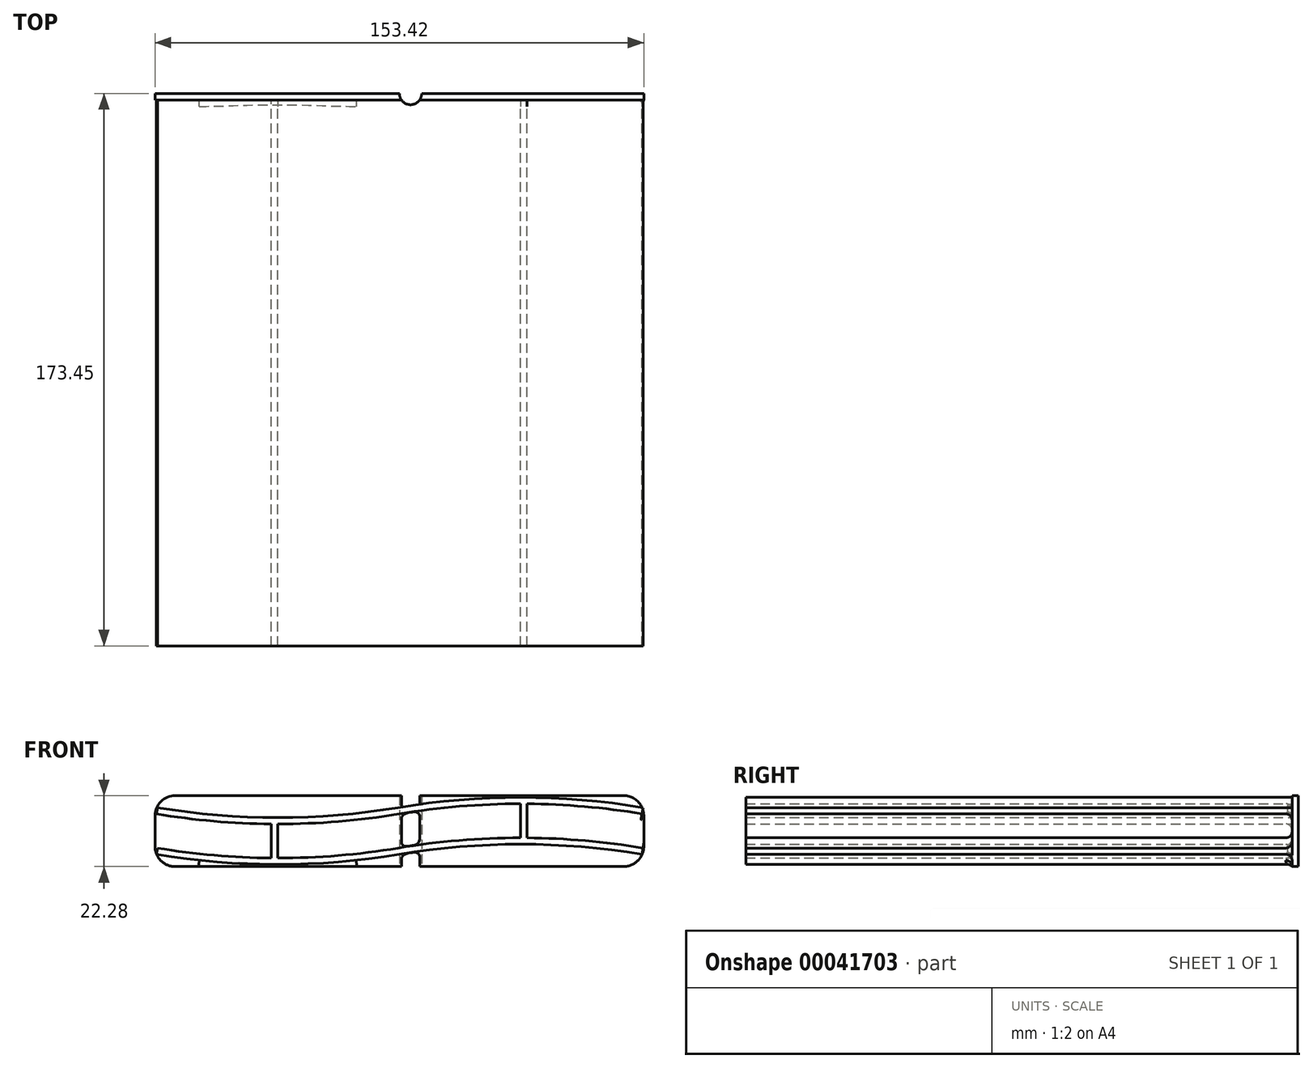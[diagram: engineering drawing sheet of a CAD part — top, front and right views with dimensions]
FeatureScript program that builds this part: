
annotation { "Feature Type Name" : "Feature", "Feature Type Description" : "" }
export const myFeature = defineFeature(function(context is Context, id is Id, definition is map)
    precondition{}
    {
        {
            var Q0;
            Q0=qCreatedBy(makeId("Front.planeOp"),FACE);
            var sketch = newSketch(context, id + "F0", { "sketchPlane" : qUnion([Q0])});
            skLineSegment(sketch, "E0", {"start": v(-48.97, -43) * mm, "end": v(27.23, -43) * mm, "construction": true});
            skLineSegment(sketch, "E1", {"start": v(27.23, -43) * mm, "end": v(103.43, -43) * mm, "construction": true});
            skPoint(sketch, "E2.1.internal.snap0", {"position": v(-10.87, -43) * mm});
            skPoint(sketch, "E2.3.internal.snap0", {"position": v(65.33, -43) * mm});
            skArc(sketch, "E3", {"start": v(-48.97, -43) * mm, "mid": v(-10.87, -46.18) * mm, "end": v(27.23, -43) * mm});
            skPoint(sketch, "E4", {"position": v(-10.87, -46.18) * mm});
            skArc(sketch, "E5", {"start": v(103.43, -43) * mm, "mid": v(65.33, -39.83) * mm, "end": v(27.23, -43) * mm});
            skPoint(sketch, "E6", {"position": v(65.33, -39.83) * mm});
            skArc(sketch, "E7.0", {"start": v(103.76, -41.03) * mm, "mid": v(85.6, -38.72) * mm, "end": v(67.33, -37.84) * mm});
            skArc(sketch, "E7.1", {"start": v(-48.64, -41.03) * mm, "mid": v(-30.82, -43.3) * mm, "end": v(-12.87, -44.17) * mm});
            skLineSegment(sketch, "E8", {"start": v(-48.64, -41.03) * mm, "end": v(-48.97, -43) * mm});
            skLineSegment(sketch, "E9", {"start": v(103.76, -41.03) * mm, "end": v(103.43, -43) * mm});
            skPoint(sketch, "E10.0.1.0", {"position": v(-10.87, -33.48) * mm});
            skArc(sketch, "E10.0.1.1", {"start": v(103.43, -30.3) * mm, "mid": v(85.44, -28) * mm, "end": v(67.33, -27.14) * mm});
            skArc(sketch, "E10.0.1.2", {"start": v(103.76, -28.33) * mm, "mid": v(65.33, -25.13) * mm, "end": v(26.9, -28.33) * mm});
            skArc(sketch, "E10.0.1.3", {"start": v(-48.97, -30.3) * mm, "mid": v(-30.99, -32.6) * mm, "end": v(-12.87, -33.47) * mm});
            skPoint(sketch, "E10.0.1.4", {"position": v(65.33, -30.3) * mm});
            skLineSegment(sketch, "E10.0.1.5", {"start": v(27.23, -30.3) * mm, "end": v(103.43, -30.3) * mm, "construction": true});
            skArc(sketch, "E10.0.1.6", {"start": v(-48.64, -28.33) * mm, "mid": v(-10.87, -31.48) * mm, "end": v(26.9, -28.33) * mm});
            skPoint(sketch, "E10.0.1.7", {"position": v(-10.87, -30.3) * mm});
            skLineSegment(sketch, "E10.0.1.8", {"start": v(-48.97, -30.3) * mm, "end": v(27.23, -30.3) * mm, "construction": true});
            skPoint(sketch, "E10.0.1.9", {"position": v(65.33, -27.13) * mm});
            skLineSegment(sketch, "E10.0.1.10", {"start": v(103.76, -28.33) * mm, "end": v(103.43, -30.3) * mm});
            skLineSegment(sketch, "E10.0.1.11", {"start": v(-48.64, -28.33) * mm, "end": v(-48.97, -30.3) * mm});
            skLineSegment(sketch, "E10.direction1", {"start": v(-10.87, -46.18) * mm, "end": v(14.53, -46.18) * mm, "construction": true});
            skLineSegment(sketch, "E10.direction2", {"start": v(-10.87, -44.18) * mm, "end": v(-10.87, -33.48) * mm, "construction": true});
            skLineSegment(sketch, "E11", {"start": v(-10.87, -33.48) * mm, "end": v(-10.87, -44.18) * mm});
            skLineSegment(sketch, "E12", {"start": v(65.33, -27.13) * mm, "end": v(65.33, -37.83) * mm});
            skLineSegment(sketch, "E13.trimOffspring", {"start": v(-12.87, -33.47) * mm, "end": v(-12.87, -44.17) * mm});
            skArc(sketch, "E14.trimOffspring", {"start": v(-10.87, -33.48) * mm, "mid": v(8.24, -32.68) * mm, "end": v(27.23, -30.3) * mm});
            skArc(sketch, "E15.trimOffspring", {"start": v(-10.87, -44.18) * mm, "mid": v(8.08, -43.4) * mm, "end": v(26.9, -41.03) * mm});
            skLineSegment(sketch, "E16", {"start": v(67.33, -27.14) * mm, "end": v(67.33, -37.84) * mm});
            skArc(sketch, "E17.trimOffspring", {"start": v(65.33, -27.13) * mm, "mid": v(46.2, -27.92) * mm, "end": v(27.23, -30.3) * mm});
            skArc(sketch, "E18.trimOffspring", {"start": v(65.33, -37.83) * mm, "mid": v(46.04, -38.63) * mm, "end": v(26.9, -41.03) * mm});
            skSolve(sketch);
        }
        {
            var Q0;
            Q0=makeQuery(id+"F0.imprint","IMPRINT",FACE,{"disambiguationData":[TD([[makeQuery(id+"F0.imprint","IMPRINT",EDGE,{"derivedFrom":sQuery(id+"F0.wireOp",EDGE,"E3")}),1.0]])]});
            extrude(context, id + "F1", {"entities" : qUnion([Q0]), "depth" : 171.45 * mm});
        }
        {
            var Q0;
            Q0=makeQuery(id+"F1.opExtrude","CAP_FACE",FACE,{"disambiguationData":[OSD([sQuery(id+"F0.wireOp",EDGE,"E3"),sQuery(id+"F0.wireOp",EDGE,"E5"),sQuery(id+"F0.wireOp",EDGE,"E7.0"),sQuery(id+"F0.wireOp",EDGE,"E7.1"),sQuery(id+"F0.wireOp",EDGE,"E8"),sQuery(id+"F0.wireOp",EDGE,"E9"),sQuery(id+"F0.wireOp",EDGE,"E10.0.1.1"),sQuery(id+"F0.wireOp",EDGE,"E10.0.1.2"),sQuery(id+"F0.wireOp",EDGE,"E10.0.1.3"),sQuery(id+"F0.wireOp",EDGE,"E10.0.1.6"),sQuery(id+"F0.wireOp",EDGE,"E10.0.1.10"),sQuery(id+"F0.wireOp",EDGE,"E10.0.1.11"),sQuery(id+"F0.wireOp",EDGE,"E11"),sQuery(id+"F0.wireOp",EDGE,"E12"),sQuery(id+"F0.wireOp",EDGE,"E13.trimOffspring"),sQuery(id+"F0.wireOp",EDGE,"E14.trimOffspring"),sQuery(id+"F0.wireOp",EDGE,"E15.trimOffspring"),sQuery(id+"F0.wireOp",EDGE,"E16"),sQuery(id+"F0.wireOp",EDGE,"E17.trimOffspring"),sQuery(id+"F0.wireOp",EDGE,"E18.trimOffspring")])],"isStart":true});
            var sketch = newSketch(context, id + "F2", { "sketchPlane" : qUnion([Q0])});
            skLineSegment(sketch, "E19.bottom", {"start": v(-97.67, -24.57) * mm, "end": v(43.05, -24.57) * mm});
            skLineSegment(sketch, "E19.top", {"start": v(-97.67, -46.85) * mm, "end": v(43.05, -46.85) * mm});
            skLineSegment(sketch, "E19.left", {"start": v(-104.02, -30.92) * mm, "end": v(-104.02, -40.5) * mm});
            skLineSegment(sketch, "E19.right", {"start": v(49.4, -30.92) * mm, "end": v(49.4, -40.5) * mm});
            skPoint(sketch, "E20.visualSharp", {"position": v(-104.02, -24.57) * mm});
            skArc(sketch, "E20.filletArc", {"start": v(-97.67, -24.57) * mm, "mid": v(-102.16, -26.43) * mm, "end": v(-104.02, -30.92) * mm});
            skPoint(sketch, "E21.visualSharp", {"position": v(-104.02, -46.85) * mm});
            skArc(sketch, "E21.filletArc", {"start": v(-104.02, -40.5) * mm, "mid": v(-102.16, -44.99) * mm, "end": v(-97.67, -46.85) * mm});
            skPoint(sketch, "E22.visualSharp", {"position": v(49.4, -24.57) * mm});
            skArc(sketch, "E22.filletArc", {"start": v(49.4, -30.92) * mm, "mid": v(47.54, -26.43) * mm, "end": v(43.05, -24.57) * mm});
            skPoint(sketch, "E23.visualSharp", {"position": v(49.4, -46.85) * mm});
            skArc(sketch, "E23.filletArc", {"start": v(43.05, -46.85) * mm, "mid": v(47.54, -44.99) * mm, "end": v(49.4, -40.5) * mm});
            skSolve(sketch);
        }
        {
            var Q0;
            Q0 = qSketchRegion(id + "F2", true);
            extrude(context, id + "F3", {"entities" : qUnion([Q0]), "operationType" : NewBodyOperationType.ADD, "depth" : 2 * mm});
        }
        {
            var Q0;
            Q0=makeQuery(id+"F1.opExtrude","CAP_EDGE",EDGE,{"disambiguationData":[OSD([sQuery(id+"F0.wireOp",EDGE,"E10.0.1.6")])],"isStart":true});
            var Q1;
            Q1=makeQuery(id+"F1.opExtrude","CAP_EDGE",EDGE,{"disambiguationData":[OSD([sQuery(id+"F0.wireOp",EDGE,"E5")])],"isStart":true});
            var Q2;
            Q2=makeQuery(id+"F1.opExtrude","CAP_EDGE",EDGE,{"disambiguationData":[OSD([sQuery(id+"F0.wireOp",EDGE,"E7.0")])],"isStart":true});
            var Q3;
            Q3=makeQuery(id+"F1.opExtrude","CAP_EDGE",EDGE,{"disambiguationData":[OSD([sQuery(id+"F0.wireOp",EDGE,"E10.0.1.1")])],"isStart":true});
            var Q4;
            Q4=makeQuery(id+"F1.opExtrude","CAP_EDGE",EDGE,{"disambiguationData":[OSD([sQuery(id+"F0.wireOp",EDGE,"E18.trimOffspring")])],"isStart":true});
            var Q5;
            Q5=makeQuery(id+"F1.opExtrude","CAP_EDGE",EDGE,{"disambiguationData":[OSD([sQuery(id+"F0.wireOp",EDGE,"E17.trimOffspring")])],"isStart":true});
            var Q6;
            Q6=makeQuery(id+"F1.opExtrude","CAP_EDGE",EDGE,{"disambiguationData":[OSD([sQuery(id+"F0.wireOp",EDGE,"E10.0.1.3")])],"isStart":true});
            var Q7;
            Q7=makeQuery(id+"F1.opExtrude","CAP_EDGE",EDGE,{"disambiguationData":[OSD([sQuery(id+"F0.wireOp",EDGE,"E7.1")])],"isStart":true});
            fillet(context, id + "F4", {"entities" : qUnion([Q0, Q1, Q2, Q3, Q4, Q5, Q6, Q7]), "radius" : 2 * mm, "tangentPropagation" : true, "allowEdgeOverflow" : false});
        }
        {
            var Q0;
            Q0=makeQuery(id+"F3.opExtrude","SWEPT_FACE",FACE,{"disambiguationData":[OSD([sQuery(id+"F2.wireOp",EDGE,"E19.top")])]});
            var sketch = newSketch(context, id + "F5", { "sketchPlane" : qUnion([Q0])});
            skArc(sketch, "E24", {"start": v(34.31, -2) * mm, "mid": v(30.81, 1.5) * mm, "end": v(27.31, -2) * mm});
            skLineSegment(sketch, "E25", {"start": v(27.31, -2) * mm, "end": v(34.31, -2) * mm});
            skSolve(sketch);
        }
        {
            var Q0;
            Q0 = qSketchRegion(id + "F5", true);
            extrude(context, id + "F6", {"entities" : qUnion([Q0]), "operationType" : NewBodyOperationType.REMOVE, "endBound" : BoundingType.THROUGH_ALL, "oppositeDirection" : true, "depth" : 25.4 * mm});
        }
    });
